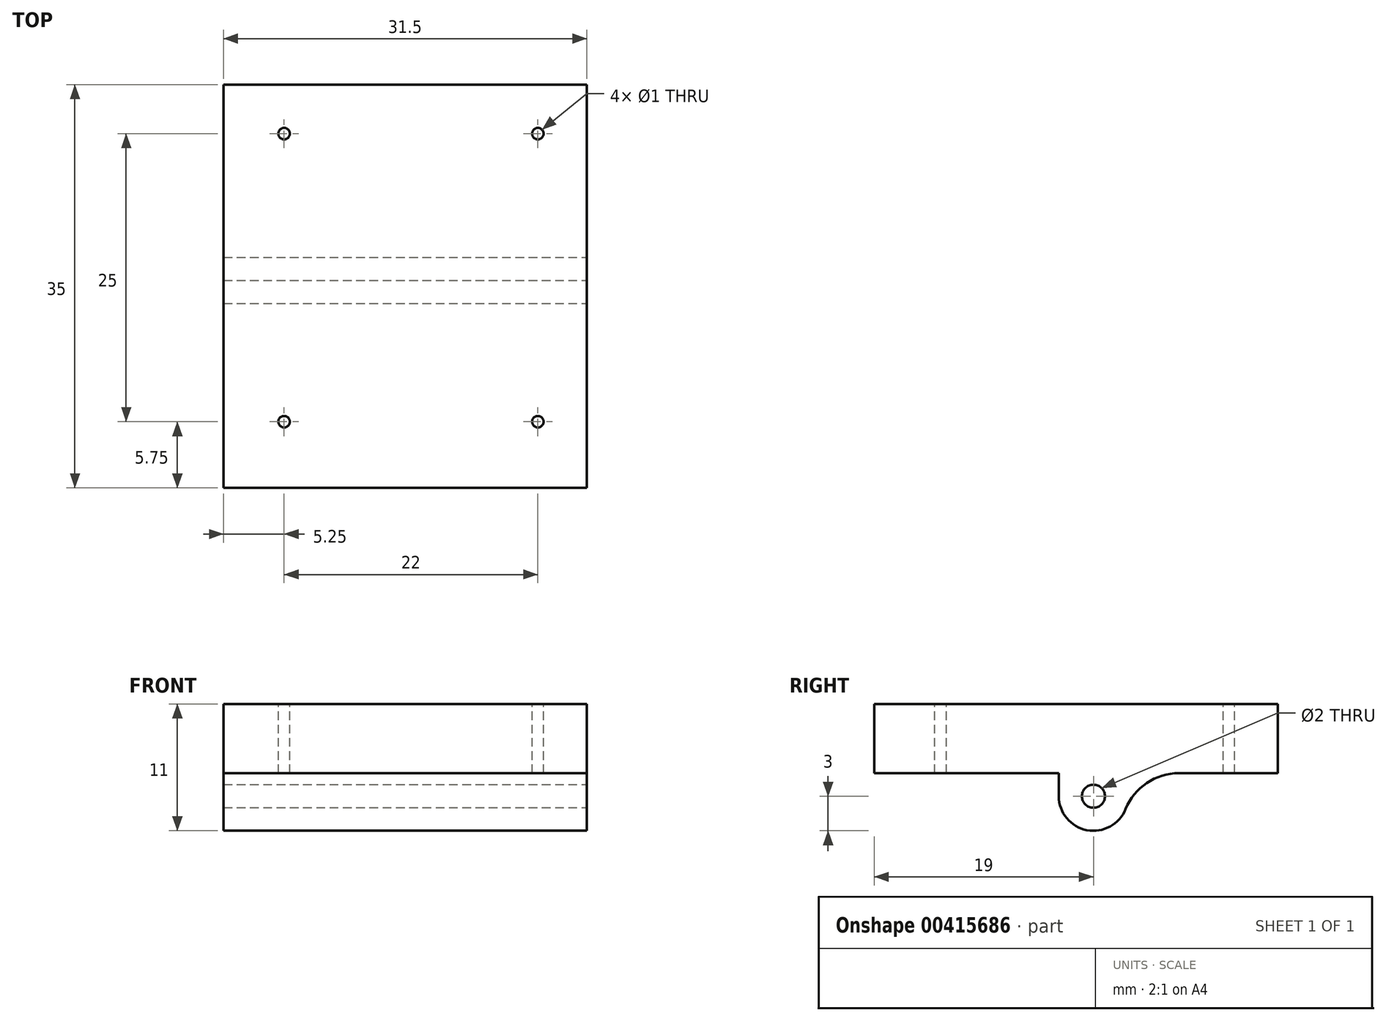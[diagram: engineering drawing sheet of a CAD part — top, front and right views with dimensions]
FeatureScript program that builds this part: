
annotation { "Feature Type Name" : "Feature", "Feature Type Description" : "" }
export const myFeature = defineFeature(function(context is Context, id is Id, definition is map)
    precondition{}
    {
        {
            var Q0;
            Q0=qCreatedBy(makeId("Top.planeOp"),FACE);
            var sketch = newSketch(context, id + "F0", { "sketchPlane" : qUnion([Q0])});
            skLineSegment(sketch, "E0.bottom", {"start": v(0, 0) * mm, "end": v(31.5, 0) * mm});
            skLineSegment(sketch, "E0.top", {"start": v(0, 35) * mm, "end": v(31.5, 35) * mm});
            skLineSegment(sketch, "E0.left", {"start": v(0, 0) * mm, "end": v(0, 35) * mm});
            skLineSegment(sketch, "E0.right", {"start": v(31.5, 0) * mm, "end": v(31.5, 35) * mm});
            skSolve(sketch);
        }
        {
            var Q0;
            Q0=makeQuery(id+"F0.imprint","IMPRINT",FACE,{"disambiguationData":[TD([[makeQuery(id+"F0.imprint","IMPRINT",EDGE,{"derivedFrom":sQuery(id+"F0.wireOp",EDGE,"E0.bottom")}),1.0]])]});
            extrude(context, id + "F1", {"entities" : qUnion([Q0]), "depth" : 6 * mm});
        }
        {
            var Q0;
            Q0=makeQuery(id+"F1.opExtrude","SWEPT_FACE",FACE,{"disambiguationData":[OSD([sQuery(id+"F0.wireOp",EDGE,"E0.right")])]});
            var sketch = newSketch(context, id + "F2", { "sketchPlane" : qUnion([Q0])});
            skLineSegment(sketch, "E1", {"start": v(19, 19.2) * mm, "end": v(19, -23.2) * mm, "construction": true});
            skPoint(sketch, "E2.oppositeSnap0", {"position": v(19, -2) * mm});
            skLineSegment(sketch, "E2.bottom", {"start": v(22, 0) * mm, "end": v(16, 0) * mm});
            skLineSegment(sketch, "E2.top", {"start": v(22, -2) * mm, "end": v(16, -2) * mm});
            skLineSegment(sketch, "E2.left", {"start": v(22, 0) * mm, "end": v(22, -2) * mm});
            skLineSegment(sketch, "E2.right", {"start": v(16, 0) * mm, "end": v(16, -2) * mm});
            skArc(sketch, "E3", {"start": v(16, -2) * mm, "mid": v(19, -5) * mm, "end": v(22, -2) * mm});
            skCircle(sketch, "E4", {"center": v(19, -2) * mm, "radius": 1 * mm});
            skSolve(sketch);
        }
        {
            var Q0;
            Q0 = qSketchRegion(id + "F2", true);
            var Q1;
            Q1=makeQuery(id+"F1.opExtrude","SWEPT_FACE",FACE,{"disambiguationData":[OSD([sQuery(id+"F0.wireOp",EDGE,"E0.left")])]});
            extrude(context, id + "F3", {"entities" : qUnion([Q0]), "operationType" : NewBodyOperationType.ADD, "endBound" : BoundingType.UP_TO_SURFACE, "oppositeDirection" : true, "endBoundEntityFace" : qUnion([Q1]), "depth" : 25 * mm});
        }
        {
            var Q0;
            Q0=makeQuery(id+"F3.opExtrude","SWEPT_EDGE",EDGE,{"disambiguationData":[OSD([sQuery(id+"F0.wireOp",EDGE,"E0.right"),sQuery(id+"F2.wireOp",EDGE,"E2.bottom"),sQuery(id+"F2.wireOp",EDGE,"E2.left")])]});
            var Q1;
            Q1=makeQuery(id+"F3.opExtrude","SWEPT_EDGE",EDGE,{"disambiguationData":[OSD([sQuery(id+"F0.wireOp",EDGE,"E0.right"),sQuery(id+"F2.wireOp",EDGE,"E2.bottom"),sQuery(id+"F2.wireOp",EDGE,"E2.right")])]});
            fillet(context, id + "F4", {"entities" : qUnion([Q0, Q1]), "radius" : 5 * mm, "tangentPropagation" : true, "allowEdgeOverflow" : false});
        }
        {
            var Q0;
            Q0=makeQuery(id+"F1.opExtrude","CAP_FACE",FACE,{"disambiguationData":[OSD([sQuery(id+"F0.wireOp",EDGE,"E0.bottom"),sQuery(id+"F0.wireOp",EDGE,"E0.top"),sQuery(id+"F0.wireOp",EDGE,"E0.left"),sQuery(id+"F0.wireOp",EDGE,"E0.right")])],"isStart":false});
            var sketch = newSketch(context, id + "F5", { "sketchPlane" : qUnion([Q0])});
            skCircle(sketch, "E5", {"center": v(27.25, 30.75) * mm, "radius": 0.5 * mm});
            skCircle(sketch, "E6.0.1.0", {"center": v(27.25, 5.75) * mm, "radius": 0.5 * mm});
            skCircle(sketch, "E6.1.0.0", {"center": v(5.25, 30.75) * mm, "radius": 0.5 * mm});
            skCircle(sketch, "E6.1.1.0", {"center": v(5.25, 5.75) * mm, "radius": 0.5 * mm});
            skLineSegment(sketch, "E6.direction1", {"start": v(27.25, 30.75) * mm, "end": v(5.25, 30.75) * mm, "construction": true});
            skLineSegment(sketch, "E6.direction2", {"start": v(27.25, 30.75) * mm, "end": v(27.25, 5.75) * mm, "construction": true});
            skSolve(sketch);
        }
        {
            var Q0;
            Q0 = qSketchRegion(id + "F5", true);
            extrude(context, id + "F6", {"entities" : qUnion([Q0]), "operationType" : NewBodyOperationType.REMOVE, "oppositeDirection" : true, "depth" : 10 * mm});
        }
    });
